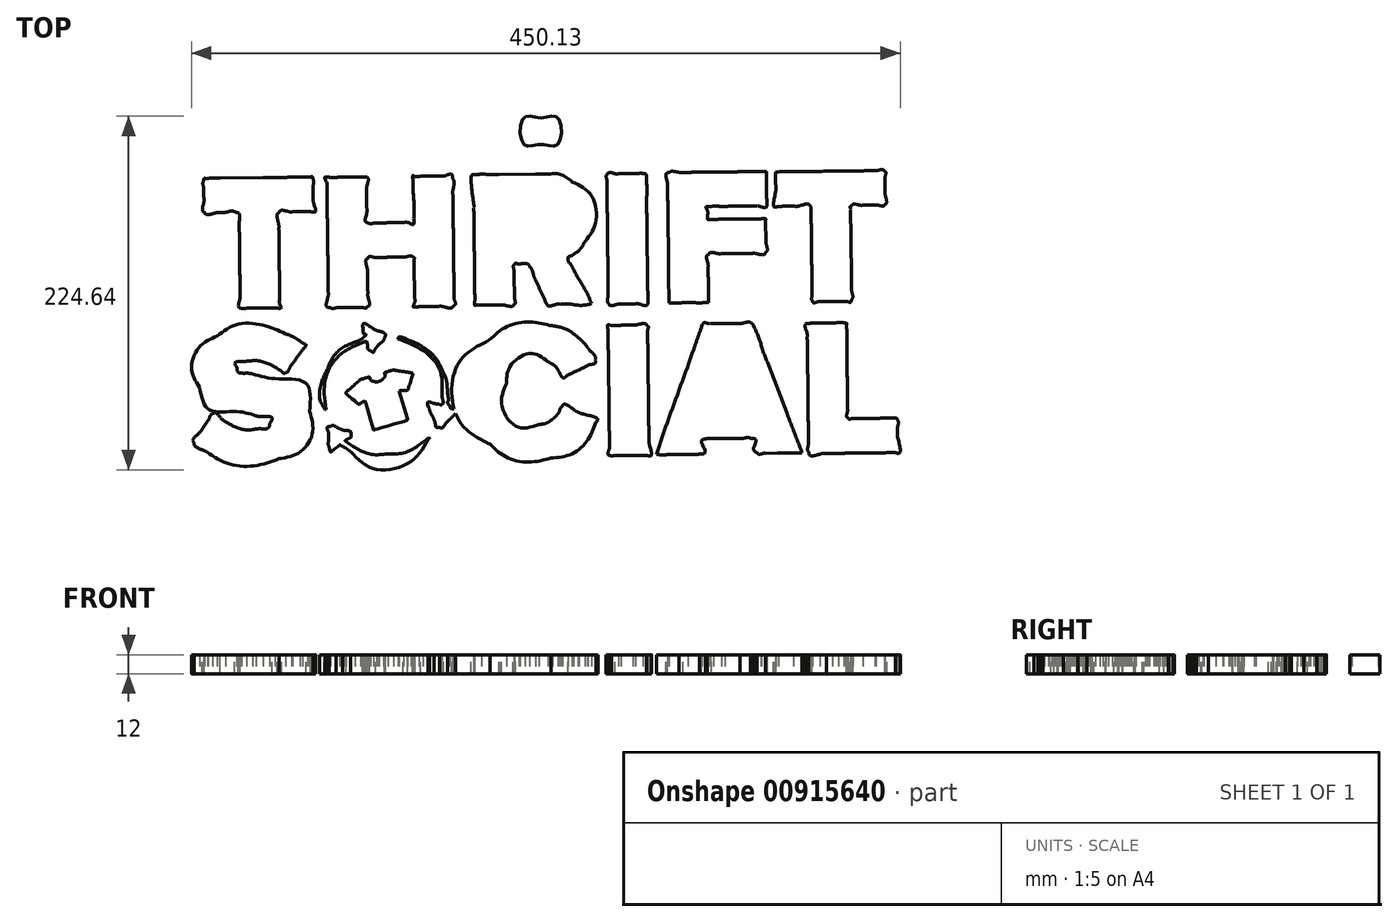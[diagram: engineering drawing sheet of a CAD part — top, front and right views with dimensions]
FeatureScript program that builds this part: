
annotation { "Feature Type Name" : "Feature", "Feature Type Description" : "" }
export const myFeature = defineFeature(function(context is Context, id is Id, definition is map)
    precondition{}
    {
        {
            var Q0;
            Q0=qCreatedBy(makeId("Top.planeOp"),FACE);
            var sketch = newSketch(context, id + "F0", { "sketchPlane" : qUnion([Q0])});
            skFitSpline(sketch, "E0", {"points": [v(237.45, -85.7) * mm, v(237.37, -79.29) * mm, v(237.62, -72.98) * mm, v(232.36, -68.27) * mm]});
            skFitSpline(sketch, "E1", {"points": [v(232.36, -68.27) * mm, v(225.56, -62.17) * mm, v(213.96, -64.54) * mm, v(205.7, -64.65) * mm]});
            skFitSpline(sketch, "E2", {"points": [v(205.7, -64.65) * mm, v(205.58, -55.22) * mm, v(205.46, -45.78) * mm, v(205.35, -36.34) * mm]});
            skFitSpline(sketch, "E3", {"points": [v(205.35, -36.34) * mm, v(205.3, -31.24) * mm, v(205.27, -26.12) * mm, v(205.19, -21.02) * mm]});
            skFitSpline(sketch, "E4", {"points": [v(205.19, -21.02) * mm, v(205.15, -18.88) * mm, v(204.58, -16.85) * mm, v(204.46, -14.77) * mm]});
            skFitSpline(sketch, "E5", {"points": [v(204.46, -14.77) * mm, v(204.35, -12.81) * mm, v(204.26, -14.2) * mm, v(205.06, -12.64) * mm]});
            skFitSpline(sketch, "E6", {"points": [v(205.06, -12.64) * mm, v(205.37, -12.05) * mm, v(205.87, -11.52) * mm, v(206.22, -10.94) * mm]});
            skFitSpline(sketch, "E7", {"points": [v(206.22, -10.94) * mm, v(208.27, -7.42) * mm, v(208.38, -3.67) * mm, v(208.32, 0.3) * mm]});
            skFitSpline(sketch, "E8", {"points": [v(208.32, 0.3) * mm, v(208.25, 4.7) * mm, v(208.24, 9.1) * mm, v(208.19, 13.51) * mm]});
            skFitSpline(sketch, "E9", {"points": [v(208.19, 13.51) * mm, v(208.08, 23.22) * mm, v(207.94, 32.92) * mm, v(207.82, 42.63) * mm]});
            skFitSpline(sketch, "E10", {"points": [v(207.82, 42.63) * mm, v(213.82, 42.68) * mm, v(219.81, 42.26) * mm, v(224.6, 46.51) * mm]});
            skFitSpline(sketch, "E11", {"points": [v(224.6, 46.51) * mm, v(228.54, 50.01) * mm, v(229.76, 54.8) * mm, v(229.7, 59.91) * mm, v(229.6, 70.09) * mm, v(232.36, 84.84) * mm, v(221.78, 90.83) * mm]});
            skFitSpline(sketch, "E12", {"points": [v(221.78, 90.83) * mm, v(216.17, 94) * mm, v(208.91, 92.77) * mm, v(202.73, 92.7) * mm]});
            skFitSpline(sketch, "E13", {"points": [v(202.73, 92.7) * mm, v(197.26, 92.62) * mm, v(191.78, 92.57) * mm, v(186.3, 92.5) * mm]});
            skFitSpline(sketch, "E14", {"points": [v(186.3, 92.5) * mm, v(179.32, 92.41) * mm, v(172.33, 92.32) * mm, v(165.34, 92.22) * mm]});
            skFitSpline(sketch, "E15", {"points": [v(165.34, 92.22) * mm, v(158.35, 92.13) * mm, v(151.35, 92.01) * mm, v(144.38, 91.73) * mm]});
            skFitSpline(sketch, "E16", {"points": [v(144.38, 91.73) * mm, v(141.8, 91.63) * mm, v(139.08, 92.28) * mm, v(136.39, 92.25) * mm]});
            skFitSpline(sketch, "E17", {"points": [v(136.39, 92.25) * mm, v(133.08, 92.2) * mm, v(129.77, 92.16) * mm, v(126.46, 92.11) * mm]});
            skFitSpline(sketch, "E18", {"points": [v(126.46, 92.11) * mm, v(112.57, 91.93) * mm, v(98.68, 91.78) * mm, v(84.79, 91.64) * mm]});
            skFitSpline(sketch, "E19", {"points": [v(84.79, 91.64) * mm, v(81.42, 91.6) * mm, v(77.86, 91.9) * mm, v(74.57, 91.06) * mm]});
            skFitSpline(sketch, "E20", {"points": [v(74.57, 91.06) * mm, v(73.32, 90.74) * mm, v(71.73, 89.56) * mm, v(70.54, 89.4) * mm]});
            skFitSpline(sketch, "E21", {"points": [v(70.54, 89.4) * mm, v(69.34, 89.25) * mm, v(67.88, 90.18) * mm, v(66.53, 90.52) * mm]});
            skFitSpline(sketch, "E22", {"points": [v(66.53, 90.52) * mm, v(60.3, 92.12) * mm, v(52.73, 90.87) * mm, v(46.32, 90.8) * mm, v(44.17, 90.77) * mm, v(42.6, 90.54) * mm, v(40.71, 91.48) * mm]});
            skFitSpline(sketch, "E23", {"points": [v(40.71, 91.48) * mm, v(37.97, 92.84) * mm, v(35.29, 94.33) * mm, v(32.58, 95.76) * mm]});
            skFitSpline(sketch, "E24", {"points": [v(32.58, 95.76) * mm, v(29.37, 97.45) * mm, v(26.16, 99.14) * mm, v(22.95, 100.83) * mm]});
            skFitSpline(sketch, "E25", {"points": [v(22.95, 100.83) * mm, v(21.58, 101.55) * mm, v(18.52, 102.46) * mm, v(17.52, 103.69) * mm]});
            skFitSpline(sketch, "E26", {"points": [v(17.52, 103.69) * mm, v(16.6, 104.82) * mm, v(16.34, 107.82) * mm, v(15.63, 109.26) * mm]});
            skFitSpline(sketch, "E27", {"points": [v(15.63, 109.26) * mm, v(14.35, 111.84) * mm, v(12.53, 114.14) * mm, v(10.34, 116) * mm]});
            skFitSpline(sketch, "E28", {"points": [v(10.34, 116) * mm, v(6.31, 119.4) * mm, v(1.07, 121.17) * mm, v(-4.18, 120.92) * mm]});
            skFitSpline(sketch, "E29", {"points": [v(-4.18, 120.92) * mm, v(-9.3, 120.68) * mm, v(-14.2, 118.52) * mm, v(-17.86, 114.94) * mm]});
            skFitSpline(sketch, "E30", {"points": [v(-17.86, 114.94) * mm, v(-19.65, 113.19) * mm, v(-21.13, 111.11) * mm, v(-22.2, 108.85) * mm]});
            skFitSpline(sketch, "E31", {"points": [v(-22.2, 108.85) * mm, v(-22.92, 107.29) * mm, v(-23.07, 104.5) * mm, v(-24.04, 103.27) * mm]});
            skFitSpline(sketch, "E32", {"points": [v(-24.04, 103.27) * mm, v(-25.28, 101.68) * mm, v(-28.46, 100.42) * mm, v(-30.14, 99.33) * mm]});
            skFitSpline(sketch, "E33", {"points": [v(-30.14, 99.33) * mm, v(-33.21, 97.35) * mm, v(-36.28, 95.38) * mm, v(-39.35, 93.4) * mm]});
            skFitSpline(sketch, "E34", {"points": [v(-39.35, 93.4) * mm, v(-40.9, 92.4) * mm, v(-42.75, 90.67) * mm, v(-44.5, 90.06) * mm]});
            skFitSpline(sketch, "E35", {"points": [v(-44.5, 90.06) * mm, v(-45.7, 89.66) * mm, v(-47.4, 89.84) * mm, v(-48.65, 89.53) * mm]});
            skFitSpline(sketch, "E36", {"points": [v(-48.65, 89.53) * mm, v(-49.89, 89.23) * mm, v(-51.05, 88.5) * mm, v(-52.25, 88.22) * mm]});
            skFitSpline(sketch, "E37", {"points": [v(-52.25, 88.22) * mm, v(-53.92, 87.84) * mm, v(-52.76, 87.94) * mm, v(-54.16, 88.18) * mm]});
            skFitSpline(sketch, "E38", {"points": [v(-54.16, 88.18) * mm, v(-54.8, 88.28) * mm, v(-55.58, 88.72) * mm, v(-56.24, 88.9) * mm]});
            skFitSpline(sketch, "E39", {"points": [v(-56.24, 88.9) * mm, v(-58.18, 89.43) * mm, v(-60.1, 89.45) * mm, v(-62.1, 89.43) * mm]});
            skFitSpline(sketch, "E40", {"points": [v(-62.1, 89.43) * mm, v(-69.08, 89.36) * mm, v(-76.1, 89.47) * mm, v(-83.08, 89.17) * mm]});
            skFitSpline(sketch, "E41", {"points": [v(-83.08, 89.17) * mm, v(-89.05, 88.92) * mm, v(-94.4, 85.9) * mm, v(-96.97, 80.38) * mm]});
            skFitSpline(sketch, "E42", {"points": [v(-96.97, 80.38) * mm, v(-97.46, 79.34) * mm, v(-97.38, 79.07) * mm, v(-98.26, 78.72) * mm]});
            skFitSpline(sketch, "E43", {"points": [v(-98.26, 78.72) * mm, v(-98.59, 78.58) * mm, v(-100.28, 78.57) * mm, v(-100.59, 78.72) * mm]});
            skFitSpline(sketch, "E44", {"points": [v(-100.59, 78.72) * mm, v(-101.26, 79.04) * mm, v(-101.72, 80.93) * mm, v(-102.2, 81.69) * mm]});
            skFitSpline(sketch, "E45", {"points": [v(-102.2, 81.69) * mm, v(-102.9, 82.8) * mm, v(-103.75, 83.83) * mm, v(-104.72, 84.73) * mm]});
            skFitSpline(sketch, "E46", {"points": [v(-104.72, 84.73) * mm, v(-109.36, 89.03) * mm, v(-115.12, 88.79) * mm, v(-121.04, 88.7) * mm]});
            skFitSpline(sketch, "E47", {"points": [v(-121.04, 88.7) * mm, v(-127.22, 88.6) * mm, v(-133.4, 88.58) * mm, v(-139.58, 88.44) * mm]});
            skFitSpline(sketch, "E48", {"points": [v(-139.58, 88.44) * mm, v(-140, 88.43) * mm, v(-140.67, 88.27) * mm, v(-141.07, 88.15) * mm]});
            skFitSpline(sketch, "E49", {"points": [v(-141.07, 88.15) * mm, v(-144.26, 87.2) * mm, v(-148.32, 88.72) * mm, v(-151.96, 88.67) * mm]});
            skFitSpline(sketch, "E50", {"points": [v(-151.96, 88.67) * mm, v(-171.27, 88.38) * mm, v(-190.58, 88.15) * mm, v(-209.9, 87.94) * mm]});
            skFitSpline(sketch, "E51", {"points": [v(-209.9, 87.94) * mm, v(-217.98, 87.85) * mm, v(-226.1, 88.6) * mm, v(-231.3, 76.87) * mm]});
            skFitSpline(sketch, "E52", {"points": [v(-231.3, 76.87) * mm, v(-231.94, 69.1) * mm, v(-231.59, 60.71) * mm, v(-231.2, 52.75) * mm]});
            skFitSpline(sketch, "E53", {"points": [v(-231.2, 52.75) * mm, v(-230.97, 47.98) * mm, v(-228.9, 43.5) * mm, v(-225, 40.65) * mm]});
            skFitSpline(sketch, "E54", {"points": [v(-225, 40.65) * mm, v(-220.14, 37.1) * mm, v(-214.44, 37.74) * mm, v(-208.76, 37.83) * mm]});
            skFitSpline(sketch, "E55", {"points": [v(-208.76, 37.83) * mm, v(-208.65, 27.45) * mm, v(-208.52, 17.06) * mm, v(-208.4, 6.68) * mm]});
            skFitSpline(sketch, "E56", {"points": [v(-208.4, 6.68) * mm, v(-208.35, 1.65) * mm, v(-208.62, -3.5) * mm, v(-208.21, -8.51) * mm]});
            skFitSpline(sketch, "E57", {"points": [v(-208.21, -8.51) * mm, v(-208.12, -9.69) * mm, v(-207.74, -10.09) * mm, v(-208.48, -10.77) * mm]});
            skFitSpline(sketch, "E58", {"points": [v(-208.48, -10.77) * mm, v(-209.04, -11.29) * mm, v(-210.44, -11.56) * mm, v(-211.13, -11.88) * mm]});
            skFitSpline(sketch, "E59", {"points": [v(-211.13, -11.88) * mm, v(-213.34, -12.88) * mm, v(-215.48, -14.04) * mm, v(-217.51, -15.37) * mm]});
            skFitSpline(sketch, "E60", {"points": [v(-217.51, -15.37) * mm, v(-230.73, -24) * mm, v(-237.84, -39.46) * mm, v(-235.49, -55.12) * mm]});
            skFitSpline(sketch, "E61", {"points": [v(-235.49, -55.12) * mm, v(-234.96, -58.61) * mm, v(-234, -62.03) * mm, v(-232.56, -65.25) * mm]});
            skFitSpline(sketch, "E62", {"points": [v(-232.56, -65.25) * mm, v(-231.7, -67.16) * mm, v(-230.68, -69) * mm, v(-229.5, -70.72) * mm]});
            skFitSpline(sketch, "E63", {"points": [v(-229.5, -70.72) * mm, v(-229.13, -71.26) * mm, v(-227.25, -73.1) * mm, v(-227.23, -73.68) * mm]});
            skFitSpline(sketch, "E64", {"points": [v(-227.23, -73.68) * mm, v(-227.2, -74.43) * mm, v(-229.05, -76.36) * mm, v(-229.44, -76.92) * mm]});
            skFitSpline(sketch, "E65", {"points": [v(-229.44, -76.92) * mm, v(-232.11, -80.84) * mm, v(-235.81, -85.02) * mm, v(-237.2, -89.63) * mm]});
            skFitSpline(sketch, "E66", {"points": [v(-237.2, -89.63) * mm, v(-242.1, -106.03) * mm, v(-218.44, -115.57) * mm, v(-206.41, -118.5) * mm]});
            skFitSpline(sketch, "E67", {"points": [v(-206.41, -118.5) * mm, v(-187.28, -123.15) * mm, v(-162.76, -122.06) * mm, v(-147.87, -107.64) * mm]});
            skFitSpline(sketch, "E68", {"points": [v(-147.87, -107.64) * mm, v(-144.82, -111.25) * mm, v(-140.15, -113.3) * mm, v(-135.43, -113.12) * mm]});
            skFitSpline(sketch, "E69", {"points": [v(-135.43, -113.12) * mm, v(-134.24, -113.08) * mm, v(-133.04, -112.9) * mm, v(-131.88, -112.58) * mm]});
            skFitSpline(sketch, "E70", {"points": [v(-131.88, -112.58) * mm, v(-130.1, -112.09) * mm, v(-130.21, -111.7) * mm, v(-128.58, -112.4) * mm]});
            skFitSpline(sketch, "E71", {"points": [v(-128.58, -112.4) * mm, v(-126.45, -113.32) * mm, v(-124.5, -114.75) * mm, v(-122.35, -115.69) * mm]});
            skFitSpline(sketch, "E72", {"points": [v(-122.35, -115.69) * mm, v(-109.58, -121.26) * mm, v(-94.53, -120.88) * mm, v(-81.82, -115.42) * mm]});
            skFitSpline(sketch, "E73", {"points": [v(-81.82, -115.42) * mm, v(-80.46, -114.83) * mm, v(-79.15, -114.14) * mm, v(-77.88, -113.37) * mm]});
            skFitSpline(sketch, "E74", {"points": [v(-77.88, -113.37) * mm, v(-72.74, -110.21) * mm, v(-67.34, -105.88) * mm, v(-63.48, -100.7) * mm]});
            skFitSpline(sketch, "E75", {"points": [v(-63.48, -100.7) * mm, v(-62.6, -99.5) * mm, v(-61.98, -98.14) * mm, v(-60.89, -97.25) * mm]});
            skFitSpline(sketch, "E76", {"points": [v(-60.89, -97.25) * mm, v(-59.3, -95.94) * mm, v(-57.34, -95.28) * mm, v(-55.76, -93.8) * mm]});
            skFitSpline(sketch, "E77", {"points": [v(-55.76, -93.8) * mm, v(-37.83, -119.87) * mm, v(2.4, -127.38) * mm, v(28, -108.14) * mm]});
            skFitSpline(sketch, "E78", {"points": [v(28, -108.14) * mm, v(32.02, -116.2) * mm, v(39.9, -116.59) * mm, v(47.86, -116.46) * mm]});
            skFitSpline(sketch, "E79", {"points": [v(47.86, -116.46) * mm, v(52.81, -116.39) * mm, v(57.77, -116.38) * mm, v(62.73, -116.3) * mm]});
            skFitSpline(sketch, "E80", {"points": [v(62.73, -116.3) * mm, v(66.12, -116.25) * mm, v(69.29, -115.58) * mm, v(72.74, -115.9) * mm]});
            skFitSpline(sketch, "E81", {"points": [v(72.74, -115.9) * mm, v(76.33, -116.24) * mm, v(79.96, -116.18) * mm, v(83.56, -115.85) * mm]});
            skFitSpline(sketch, "E82", {"points": [v(83.56, -115.85) * mm, v(93.02, -115) * mm, v(104.6, -117.99) * mm, v(110.6, -108.36) * mm]});
            skFitSpline(sketch, "E83", {"points": [v(110.6, -108.36) * mm, v(110.87, -107.93) * mm, v(111.19, -107.02) * mm, v(111.55, -106.61) * mm]});
            skFitSpline(sketch, "E84", {"points": [v(111.55, -106.61) * mm, v(112.6, -105.43) * mm, v(112.76, -105.67) * mm, v(114.58, -105.66) * mm]});
            skFitSpline(sketch, "E85", {"points": [v(114.58, -105.66) * mm, v(115.87, -105.64) * mm, v(117.16, -105.63) * mm, v(118.46, -105.62) * mm]});
            skFitSpline(sketch, "E86", {"points": [v(118.46, -105.62) * mm, v(120.23, -105.6) * mm, v(120.37, -105.35) * mm, v(121.42, -106.5) * mm]});
            skFitSpline(sketch, "E87", {"points": [v(121.42, -106.5) * mm, v(122.48, -107.63) * mm, v(123.04, -109.24) * mm, v(124.18, -110.4) * mm]});
            skFitSpline(sketch, "E88", {"points": [v(124.18, -110.4) * mm, v(125.7, -112) * mm, v(127.58, -113.22) * mm, v(129.64, -114.01) * mm]});
            skFitSpline(sketch, "E89", {"points": [v(129.64, -114.01) * mm, v(134.17, -115.74) * mm, v(139.1, -114.75) * mm, v(143.77, -115.03) * mm]});
            skFitSpline(sketch, "E90", {"points": [v(143.77, -115.03) * mm, v(146.14, -115.17) * mm, v(148.5, -115.08) * mm, v(150.87, -114.97) * mm]});
            skFitSpline(sketch, "E91", {"points": [v(150.87, -114.97) * mm, v(162.8, -114.43) * mm, v(174.77, -115.11) * mm, v(186.82, -114.99) * mm]});
            skFitSpline(sketch, "E92", {"points": [v(186.82, -114.99) * mm, v(190.81, -114.95) * mm, v(194.8, -114.9) * mm, v(198.8, -114.86) * mm]});
            skFitSpline(sketch, "E93", {"points": [v(198.8, -114.86) * mm, v(203.91, -114.8) * mm, v(209.03, -114.74) * mm, v(214.14, -114.67) * mm]});
            skFitSpline(sketch, "E94", {"points": [v(214.14, -114.67) * mm, v(219.16, -114.6) * mm, v(224.67, -115.22) * mm, v(229.3, -112.93) * mm]});
            skFitSpline(sketch, "E95", {"points": [v(229.3, -112.93) * mm, v(239.81, -107.74) * mm, v(237.57, -95.35) * mm, v(237.45, -85.7) * mm]});
            skFitSpline(sketch, "E96", {"points": [v(-169.5, -104.3) * mm, v(-184.03, -108.7) * mm, v(-201.82, -107.43) * mm, v(-215.22, -100.1) * mm]});
            skFitSpline(sketch, "E97", {"points": [v(-215.22, -100.1) * mm, v(-217.04, -99.1) * mm, v(-222.72, -96.5) * mm, v(-223.4, -94.41) * mm]});
            skFitSpline(sketch, "E98", {"points": [v(-223.4, -94.41) * mm, v(-224.13, -92.16) * mm, v(-219.57, -87.52) * mm, v(-218.25, -85.59) * mm]});
            skFitSpline(sketch, "E99", {"points": [v(-218.25, -85.59) * mm, v(-217.09, -83.89) * mm, v(-215.93, -82.18) * mm, v(-214.77, -80.48) * mm]});
            skFitSpline(sketch, "E100", {"points": [v(-214.77, -80.48) * mm, v(-214.12, -79.52) * mm, v(-212.76, -76.37) * mm, v(-211.6, -75.9) * mm]});
            skFitSpline(sketch, "E101", {"points": [v(-211.6, -75.9) * mm, v(-209.8, -75.16) * mm, v(-205.2, -79.76) * mm, v(-203.38, -80.77) * mm]});
            skFitSpline(sketch, "E102", {"points": [v(-203.38, -80.77) * mm, v(-197.56, -84.02) * mm, v(-190.4, -85.96) * mm, v(-183.7, -85.45) * mm]});
            skFitSpline(sketch, "E103", {"points": [v(-183.7, -85.45) * mm, v(-181.24, -85.26) * mm, v(-176.38, -84.97) * mm, v(-175.4, -82.06) * mm]});
            skFitSpline(sketch, "E104", {"points": [v(-175.4, -82.06) * mm, v(-174.05, -78.03) * mm, v(-181.49, -77.57) * mm, v(-183.9, -77.07) * mm]});
            skFitSpline(sketch, "E105", {"points": [v(-183.9, -77.07) * mm, v(-196.85, -74.39) * mm, v(-213.89, -73.12) * mm, v(-219.86, -59.08) * mm]});
            skFitSpline(sketch, "E106", {"points": [v(-219.86, -59.08) * mm, v(-225, -47) * mm, v(-219.75, -33.1) * mm, v(-208.69, -26.5) * mm]});
            skFitSpline(sketch, "E107", {"points": [v(-208.69, -26.5) * mm, v(-196.07, -19) * mm, v(-178.57, -19.8) * mm, v(-165.25, -24.97) * mm]});
            skFitSpline(sketch, "E108", {"points": [v(-165.25, -24.97) * mm, v(-162.09, -26.2) * mm, v(-159.06, -27.74) * mm, v(-156.2, -29.57) * mm]});
            skFitSpline(sketch, "E109", {"points": [v(-156.2, -29.57) * mm, v(-153.01, -31.62) * mm, v(-152.16, -31.98) * mm, v(-154.52, -35.2) * mm]});
            skFitSpline(sketch, "E110", {"points": [v(-154.52, -35.2) * mm, v(-156.85, -38.38) * mm, v(-159.2, -41.54) * mm, v(-161.53, -44.71) * mm]});
            skFitSpline(sketch, "E111", {"points": [v(-161.53, -44.71) * mm, v(-162.25, -45.7) * mm, v(-163.98, -49.06) * mm, v(-165.15, -49.55) * mm]});
            skFitSpline(sketch, "E112", {"points": [v(-165.15, -49.55) * mm, v(-166.52, -50.13) * mm, v(-167.86, -48.73) * mm, v(-169.03, -48.04) * mm]});
            skFitSpline(sketch, "E113", {"points": [v(-169.03, -48.04) * mm, v(-175.33, -44.34) * mm, v(-182.8, -42.13) * mm, v(-190.16, -42.42) * mm]});
            skFitSpline(sketch, "E114", {"points": [v(-190.16, -42.42) * mm, v(-192.3, -42.5) * mm, v(-197.37, -43.22) * mm, v(-196.2, -46.55) * mm]});
            skFitSpline(sketch, "E115", {"points": [v(-196.2, -46.55) * mm, v(-195.2, -49.47) * mm, v(-188.8, -50.03) * mm, v(-186.2, -50.55) * mm]});
            skFitSpline(sketch, "E116", {"points": [v(-186.2, -50.55) * mm, v(-171.68, -53.46) * mm, v(-152.42, -56.36) * mm, v(-150.06, -74.27) * mm]});
            skFitSpline(sketch, "E117", {"points": [v(-150.06, -74.27) * mm, v(-148.25, -87.95) * mm, v(-156.37, -100.3) * mm, v(-169.5, -104.3) * mm]});
            skFitSpline(sketch, "E118", {"points": [v(-149.46, 52.65) * mm, v(-153.23, 52.65) * mm, v(-157, 52.6) * mm, v(-160.78, 52.55) * mm]});
            skFitSpline(sketch, "E119", {"points": [v(-160.78, 52.55) * mm, v(-162.7, 52.53) * mm, v(-168.01, 53.44) * mm, v(-169.45, 51.94) * mm]});
            skFitSpline(sketch, "E120", {"points": [v(-169.45, 51.94) * mm, v(-170.73, 50.61) * mm, v(-169.61, 44.07) * mm, v(-169.59, 42.3) * mm]});
            skFitSpline(sketch, "E121", {"points": [v(-169.59, 42.3) * mm, v(-169.54, 38.57) * mm, v(-169.5, 34.85) * mm, v(-169.45, 31.12) * mm]});
            skFitSpline(sketch, "E122", {"points": [v(-169.45, 31.12) * mm, v(-169.36, 23.66) * mm, v(-169.27, 16.2) * mm, v(-169.2, 8.74) * mm]});
            skFitSpline(sketch, "E123", {"points": [v(-169.2, 8.74) * mm, v(-169.15, 4.96) * mm, v(-169.11, 1.2) * mm, v(-169.06, -2.58) * mm]});
            skFitSpline(sketch, "E124", {"points": [v(-169.06, -2.58) * mm, v(-169.01, -6.06) * mm, v(-168, -8.45) * mm, v(-172, -8.55) * mm]});
            skFitSpline(sketch, "E125", {"points": [v(-172, -8.55) * mm, v(-175.65, -8.64) * mm, v(-179.3, -8.6) * mm, v(-182.95, -8.65) * mm]});
            skFitSpline(sketch, "E126", {"points": [v(-182.95, -8.65) * mm, v(-186.36, -8.7) * mm, v(-189.76, -8.75) * mm, v(-193.16, -8.82) * mm]});
            skFitSpline(sketch, "E127", {"points": [v(-193.16, -8.82) * mm, v(-195.24, -7.83) * mm, v(-194.19, -2.27) * mm, v(-194.2, -0.21) * mm]});
            skFitSpline(sketch, "E128", {"points": [v(-194.2, -0.21) * mm, v(-194.25, 3.55) * mm, v(-194.3, 7.3) * mm, v(-194.33, 11.07) * mm]});
            skFitSpline(sketch, "E129", {"points": [v(-194.33, 11.07) * mm, v(-194.42, 18.58) * mm, v(-194.5, 26.1) * mm, v(-194.59, 33.62) * mm]});
            skFitSpline(sketch, "E130", {"points": [v(-194.59, 33.62) * mm, v(-194.63, 37.38) * mm, v(-194.67, 41.14) * mm, v(-194.7, 44.9) * mm]});
            skFitSpline(sketch, "E131", {"points": [v(-194.7, 44.9) * mm, v(-194.72, 46.17) * mm, v(-194.46, 47.8) * mm, v(-194.54, 49.21) * mm]});
            skFitSpline(sketch, "E132", {"points": [v(-194.54, 49.21) * mm, v(-194.63, 50.61) * mm, v(-195.07, 51.8) * mm, v(-196.49, 52.16) * mm]});
            skFitSpline(sketch, "E133", {"points": [v(-196.49, 52.16) * mm, v(-199.58, 52.95) * mm, v(-204.12, 52.03) * mm, v(-207.33, 51.98) * mm]});
            skFitSpline(sketch, "E134", {"points": [v(-207.33, 51.98) * mm, v(-209.27, 51.95) * mm, v(-215.39, 50.77) * mm, v(-216.77, 52.14) * mm]});
            skFitSpline(sketch, "E135", {"points": [v(-216.77, 52.14) * mm, v(-218.06, 53.43) * mm, v(-217.16, 58.96) * mm, v(-217.19, 60.73) * mm]});
            skFitSpline(sketch, "E136", {"points": [v(-217.19, 60.73) * mm, v(-217.21, 62.5) * mm, v(-217.25, 64.26) * mm, v(-217.29, 66.03) * mm]});
            skFitSpline(sketch, "E137", {"points": [v(-217.29, 66.03) * mm, v(-217.32, 67.73) * mm, v(-217.88, 70.35) * mm, v(-217.43, 71.98) * mm]});
            skFitSpline(sketch, "E138", {"points": [v(-217.43, 71.98) * mm, v(-216.94, 73.8) * mm, v(-216.2, 73.73) * mm, v(-214.58, 73.77) * mm]});
            skFitSpline(sketch, "E139", {"points": [v(-214.58, 73.77) * mm, v(-212.04, 73.84) * mm, v(-209.5, 73.8) * mm, v(-206.95, 73.89) * mm]});
            skFitSpline(sketch, "E140", {"points": [v(-206.95, 73.89) * mm, v(-197.85, 74.03) * mm, v(-188.74, 74.16) * mm, v(-179.63, 74.3) * mm]});
            skFitSpline(sketch, "E141", {"points": [v(-179.63, 74.3) * mm, v(-170.17, 74.22) * mm, v(-160.7, 74.51) * mm, v(-151.23, 74.56) * mm]});
            skFitSpline(sketch, "E142", {"points": [v(-151.23, 74.56) * mm, v(-149.73, 74.57) * mm, v(-148.42, 74.88) * mm, v(-147.88, 73.2) * mm]});
            skFitSpline(sketch, "E143", {"points": [v(-147.88, 73.2) * mm, v(-147.35, 71.56) * mm, v(-147.83, 68.9) * mm, v(-147.81, 67.19) * mm]});
            skFitSpline(sketch, "E144", {"points": [v(-147.81, 67.19) * mm, v(-147.8, 65.07) * mm, v(-147.77, 62.94) * mm, v(-147.74, 60.82) * mm]});
            skFitSpline(sketch, "E145", {"points": [v(-147.74, 60.82) * mm, v(-147.7, 58.78) * mm, v(-146.23, 52.64) * mm, v(-149.46, 52.65) * mm]});
            skFitSpline(sketch, "E146", {"points": [v(-137, 74.37) * mm, v(-133.2, 74.42) * mm, v(-129.4, 74.45) * mm, v(-125.6, 74.5) * mm]});
            skFitSpline(sketch, "E147", {"points": [v(-125.6, 74.5) * mm, v(-122.04, 74.55) * mm, v(-118.48, 74.6) * mm, v(-114.92, 74.68) * mm]});
            skFitSpline(sketch, "E148", {"points": [v(-114.92, 74.68) * mm, v(-112.8, 73.7) * mm, v(-113.89, 67.74) * mm, v(-113.86, 65.59) * mm]});
            skFitSpline(sketch, "E149", {"points": [v(-113.86, 65.59) * mm, v(-113.8, 61.71) * mm, v(-113.74, 57.84) * mm, v(-113.7, 53.97) * mm]});
            skFitSpline(sketch, "E150", {"points": [v(-113.7, 53.97) * mm, v(-113.67, 52.07) * mm, v(-114.65, 46.45) * mm, v(-112.7, 45.43) * mm, v(-111.67, 44.9) * mm, v(-109.32, 45.37) * mm, v(-108.24, 45.4) * mm]});
            skFitSpline(sketch, "E151", {"points": [v(-108.24, 45.4) * mm, v(-105.97, 45.44) * mm, v(-103.69, 45.48) * mm, v(-101.4, 45.52) * mm]});
            skFitSpline(sketch, "E152", {"points": [v(-101.4, 45.52) * mm, v(-97.76, 45.58) * mm, v(-94.12, 45.62) * mm, v(-90.47, 45.66) * mm]});
            skFitSpline(sketch, "E153", {"points": [v(-90.47, 45.66) * mm, v(-87.46, 45.69) * mm, v(-84.08, 44.55) * mm, v(-83.93, 48.22) * mm]});
            skFitSpline(sketch, "E154", {"points": [v(-83.93, 48.22) * mm, v(-83.62, 55.92) * mm, v(-84.16, 63.76) * mm, v(-84.3, 71.46) * mm]});
            skFitSpline(sketch, "E155", {"points": [v(-84.3, 71.46) * mm, v(-84.36, 75.55) * mm, v(-83.3, 75.05) * mm, v(-79.42, 75.09) * mm]});
            skFitSpline(sketch, "E156", {"points": [v(-79.42, 75.09) * mm, v(-75.21, 75.13) * mm, v(-71, 75.18) * mm, v(-66.78, 75.24) * mm]});
            skFitSpline(sketch, "E157", {"points": [v(-66.78, 75.24) * mm, v(-64.22, 75.27) * mm, v(-59.98, 76.5) * mm, v(-59.13, 73.73) * mm]});
            skFitSpline(sketch, "E158", {"points": [v(-59.13, 73.73) * mm, v(-58.21, 70.77) * mm, v(-59.04, 66.1) * mm, v(-59, 62.98) * mm]});
            skFitSpline(sketch, "E159", {"points": [v(-59, 62.98) * mm, v(-58.91, 55.12) * mm, v(-58.83, 47.27) * mm, v(-58.75, 39.4) * mm]});
            skFitSpline(sketch, "E160", {"points": [v(-58.75, 39.4) * mm, v(-58.66, 31.3) * mm, v(-58.57, 23.19) * mm, v(-58.47, 15.08) * mm]});
            skFitSpline(sketch, "E161", {"points": [v(-58.47, 15.08) * mm, v(-58.43, 11.37) * mm, v(-58.39, 7.66) * mm, v(-58.33, 3.95) * mm]});
            skFitSpline(sketch, "E162", {"points": [v(-58.33, 3.95) * mm, v(-58.3, 2.1) * mm, v(-58.27, 0.24) * mm, v(-58.23, -1.62) * mm]});
            skFitSpline(sketch, "E163", {"points": [v(-58.23, -1.62) * mm, v(-58.2, -2.92) * mm, v(-57.4, -6.18) * mm, v(-58.5, -7.15) * mm]});
            skFitSpline(sketch, "E164", {"points": [v(-58.5, -7.15) * mm, v(-60.11, -8.57) * mm, v(-66, -7.55) * mm, v(-68.1, -7.57) * mm]});
            skFitSpline(sketch, "E165", {"points": [v(-68.1, -7.57) * mm, v(-70.18, -7.6) * mm, v(-72.26, -7.65) * mm, v(-74.34, -7.7) * mm]});
            skFitSpline(sketch, "E166", {"points": [v(-74.34, -7.7) * mm, v(-76.42, -7.73) * mm, v(-78.5, -7.77) * mm, v(-80.57, -7.75) * mm]});
            skFitSpline(sketch, "E167", {"points": [v(-80.57, -7.75) * mm, v(-84.3, -7.72) * mm, v(-83.32, -5.38) * mm, v(-83.37, -2.15) * mm]});
            skFitSpline(sketch, "E168", {"points": [v(-83.37, -2.15) * mm, v(-83.42, 1.94) * mm, v(-83.49, 6.02) * mm, v(-83.54, 10.11) * mm]});
            skFitSpline(sketch, "E169", {"points": [v(-83.54, 10.11) * mm, v(-83.6, 13.78) * mm, v(-83.57, 17.46) * mm, v(-83.66, 21.14) * mm]});
            skFitSpline(sketch, "E170", {"points": [v(-83.66, 21.14) * mm, v(-83.68, 22.15) * mm, v(-83.4, 23.24) * mm, v(-84.37, 23.8) * mm]});
            skFitSpline(sketch, "E171", {"points": [v(-84.37, 23.8) * mm, v(-85.68, 24.55) * mm, v(-89.15, 23.8) * mm, v(-90.67, 23.77) * mm]});
            skFitSpline(sketch, "E172", {"points": [v(-90.67, 23.77) * mm, v(-94.44, 23.7) * mm, v(-98.2, 23.65) * mm, v(-101.98, 23.6) * mm]});
            skFitSpline(sketch, "E173", {"points": [v(-101.98, 23.6) * mm, v(-103.86, 23.57) * mm, v(-105.74, 23.55) * mm, v(-107.63, 23.53) * mm]});
            skFitSpline(sketch, "E174", {"points": [v(-107.63, 23.53) * mm, v(-108.89, 23.51) * mm, v(-112.1, 24.1) * mm, v(-113.04, 23.1) * mm]});
            skFitSpline(sketch, "E175", {"points": [v(-113.04, 23.1) * mm, v(-114.32, 21.73) * mm, v(-113.22, 15.28) * mm, v(-113.2, 13.41) * mm]});
            skFitSpline(sketch, "E176", {"points": [v(-113.2, 13.41) * mm, v(-113.15, 9.16) * mm, v(-113.1, 4.92) * mm, v(-113.05, 0.67) * mm]});
            skFitSpline(sketch, "E177", {"points": [v(-113.05, 0.67) * mm, v(-113.02, -1.3) * mm, v(-111.94, -6.5) * mm, v(-113.48, -7.95) * mm]});
            skFitSpline(sketch, "E178", {"points": [v(-113.48, -7.95) * mm, v(-114.24, -8.66) * mm, v(-116.43, -8.19) * mm, v(-117.38, -8.2) * mm]});
            skFitSpline(sketch, "E179", {"points": [v(-117.38, -8.2) * mm, v(-119.64, -8.21) * mm, v(-121.9, -8.23) * mm, v(-124.17, -8.26) * mm, v(-126.44, -8.28) * mm, v(-128.7, -8.31) * mm, v(-130.97, -8.35) * mm]});
            skFitSpline(sketch, "E180", {"points": [v(-130.97, -8.35) * mm, v(-132.57, -8.37) * mm, v(-135.32, -8.94) * mm, v(-136.83, -8.4) * mm]});
            skFitSpline(sketch, "E181", {"points": [v(-136.83, -8.4) * mm, v(-139.37, -7.5) * mm, v(-138.2, -0.8) * mm, v(-138.22, 1.59) * mm]});
            skFitSpline(sketch, "E182", {"points": [v(-138.22, 1.59) * mm, v(-138.3, 10.29) * mm, v(-138.4, 18.99) * mm, v(-138.5, 27.69) * mm]});
            skFitSpline(sketch, "E183", {"points": [v(-138.5, 27.69) * mm, v(-138.6, 36.73) * mm, v(-138.74, 45.78) * mm, v(-138.86, 54.83) * mm]});
            skFitSpline(sketch, "E184", {"points": [v(-138.86, 54.83) * mm, v(-138.92, 59.25) * mm, v(-138.98, 63.67) * mm, v(-139.04, 68.1) * mm]});
            skFitSpline(sketch, "E185", {"points": [v(-139.04, 68.1) * mm, v(-139.07, 70.76) * mm, v(-140.38, 74.33) * mm, v(-137, 74.37) * mm]});
            skFitSpline(sketch, "E186", {"points": [v(-87.99, -78.97) * mm, v(-87.81, -79.58) * mm, v(-88.06, -79.98) * mm, v(-88.73, -80.18) * mm, v(-88.74, -80.18) * mm, v(-88.78, -80.2) * mm, v(-108.5, -85.88) * mm, v(-108.55, -85.9) * mm, v(-108.55, -85.9) * mm, v(-109.16, -86.07) * mm, v(-109.56, -85.85) * mm, v(-109.73, -85.24) * mm, v(-109.73, -85.24) * mm, v(-109.74, -85.2) * mm, v(-114.75, -67.68) * mm, v(-114.81, -67.45) * mm, v(-114.81, -67.45) * mm, v(-114.81, -67.45) * mm]});
            skFitSpline(sketch, "E187", {"points": [v(-114.81, -67.45) * mm, v(-114.82, -67.45) * mm, v(-114.82, -67.45) * mm, v(-114.9, -67.5) * mm, v(-118.22, -69.42) * mm, v(-118.24, -69.43) * mm, v(-118.24, -69.43) * mm, v(-118.62, -69.73) * mm, v(-118.99, -69.7) * mm, v(-119.36, -69.35) * mm, v(-119.36, -69.35) * mm, v(-119.4, -69.32) * mm, v(-126.54, -63.31) * mm, v(-126.57, -63.3) * mm, v(-126.58, -63.29) * mm, v(-126.77, -63.08) * mm, v(-126.87, -62.84) * mm, v(-126.87, -62.58) * mm]});
            skFitSpline(sketch, "E188", {"points": [v(-126.87, -62.58) * mm, v(-126.9, -62.26) * mm, v(-126.78, -62) * mm, v(-126.5, -61.79) * mm, v(-126.5, -61.78) * mm, v(-126.47, -61.75) * mm, v(-117.78, -54.07) * mm, v(-117.67, -53.97) * mm, v(-117.67, -53.97) * mm, v(-117.67, -53.97) * mm]});
            skFitSpline(sketch, "E189", {"points": [v(-117.67, -53.97) * mm, v(-117.67, -53.97) * mm, v(-117.67, -53.97) * mm, v(-117.54, -53.94) * mm, v(-112.88, -52.6) * mm, v(-112.88, -52.6) * mm, v(-112.87, -52.6) * mm, v(-112.26, -52.42) * mm, v(-111.87, -52.63) * mm, v(-111.7, -53.24) * mm]});
            skFitSpline(sketch, "E190", {"points": [v(-111.7, -53.24) * mm, v(-111.43, -54.16) * mm, v(-110.7, -54.8) * mm, v(-109.5, -55.14) * mm]});
            skFitSpline(sketch, "E191", {"points": [v(-109.5, -55.14) * mm, v(-108.3, -55.5) * mm, v(-107.17, -55.51) * mm, v(-106.1, -55.2) * mm]});
            skFitSpline(sketch, "E192", {"points": [v(-106.1, -55.2) * mm, v(-105.02, -54.9) * mm, v(-104.05, -54.27) * mm, v(-103.2, -53.32) * mm]});
            skFitSpline(sketch, "E193", {"points": [v(-103.2, -53.32) * mm, v(-102.33, -52.38) * mm, v(-102.03, -51.45) * mm, v(-102.3, -50.53) * mm]});
            skFitSpline(sketch, "E194", {"points": [v(-102.3, -50.53) * mm, v(-102.47, -49.93) * mm, v(-102.25, -49.53) * mm, v(-101.64, -49.35) * mm, v(-101.63, -49.35) * mm, v(-101.63, -49.35) * mm, v(-96.97, -48) * mm, v(-96.84, -47.97) * mm, v(-96.84, -47.97) * mm, v(-96.84, -47.97) * mm]});
            skFitSpline(sketch, "E195", {"points": [v(-96.84, -47.97) * mm, v(-96.84, -47.97) * mm, v(-96.84, -47.97) * mm, v(-96.7, -48) * mm, v(-85.4, -49.81) * mm, v(-85.35, -49.82) * mm, v(-85.34, -49.82) * mm, v(-85, -49.85) * mm, v(-84.76, -50.02) * mm, v(-84.6, -50.3) * mm]});
            skFitSpline(sketch, "E196", {"points": [v(-84.6, -50.3) * mm, v(-84.48, -50.53) * mm, v(-84.46, -50.82) * mm, v(-84.56, -51.17) * mm, v(-84.56, -51.18) * mm, v(-84.57, -51.21) * mm, v(-87.47, -60.13) * mm, v(-87.48, -60.16) * mm, v(-87.48, -60.16) * mm, v(-87.58, -60.52) * mm, v(-87.84, -60.76) * mm, v(-88.27, -60.88) * mm]});
            skFitSpline(sketch, "E197", {"points": [v(-88.27, -60.88) * mm, v(-88.45, -60.94) * mm, v(-88.6, -60.95) * mm, v(-88.75, -60.93) * mm, v(-88.75, -60.93) * mm, v(-88.79, -60.93) * mm, v(-92.96, -61.17) * mm, v(-93.07, -61.18) * mm, v(-93.07, -61.18) * mm, v(-93.07, -61.18) * mm]});
            skFitSpline(sketch, "E198", {"points": [v(-93.07, -61.18) * mm, v(-93.07, -61.18) * mm, v(-93.07, -61.18) * mm, v(-93, -61.4) * mm, v(-88.05, -78.74) * mm, v(-87.99, -78.97) * mm, v(-87.99, -78.97) * mm, v(-87.99, -78.97) * mm]});
            skFitSpline(sketch, "E199", {"points": [v(-140.1, -73) * mm, v(-143.69, -65.5) * mm, v(-142.17, -55.1) * mm, v(-138.83, -47.81) * mm]});
            skFitSpline(sketch, "E200", {"points": [v(-138.83, -47.81) * mm, v(-135.32, -40.12) * mm, v(-128.95, -33.71) * mm, v(-121.2, -30.3) * mm]});
            skFitSpline(sketch, "E201", {"points": [v(-121.2, -30.3) * mm, v(-119.65, -29.62) * mm, v(-116.64, -28.05) * mm, v(-115.6, -26.93) * mm]});
            skFitSpline(sketch, "E202", {"points": [v(-115.6, -26.93) * mm, v(-114.22, -25.44) * mm, v(-116.03, -24.6) * mm, v(-115.95, -22.87) * mm]});
            skFitSpline(sketch, "E203", {"points": [v(-115.95, -22.87) * mm, v(-115.75, -18.46) * mm, v(-108.36, -22.42) * mm, v(-105.94, -23.23) * mm]});
            skFitSpline(sketch, "E204", {"points": [v(-105.94, -23.23) * mm, v(-104.9, -23.58) * mm, v(-103.73, -23.84) * mm, v(-102.94, -24.34) * mm]});
            skFitSpline(sketch, "E205", {"points": [v(-102.94, -24.34) * mm, v(-102.15, -24.85) * mm, v(-101.74, -25.6) * mm, v(-102.21, -26.91) * mm]});
            skFitSpline(sketch, "E206", {"points": [v(-102.21, -26.91) * mm, v(-102.96, -28.98) * mm, v(-105.72, -31.4) * mm, v(-107.13, -33.09) * mm]});
            skFitSpline(sketch, "E207", {"points": [v(-107.13, -33.09) * mm, v(-108.19, -34.35) * mm, v(-109.55, -36.7) * mm, v(-111.4, -35.6) * mm]});
            skFitSpline(sketch, "E208", {"points": [v(-111.4, -35.6) * mm, v(-112.95, -34.7) * mm, v(-113.42, -31.08) * mm, v(-113.9, -29.6) * mm]});
            skFitSpline(sketch, "E209", {"points": [v(-113.9, -29.6) * mm, v(-130.83, -38.37) * mm, v(-140.09, -54) * mm, v(-139.65, -73.05) * mm]});
            skFitSpline(sketch, "E210", {"points": [v(-139.65, -73.05) * mm, v(-139.8, -73.03) * mm, v(-139.96, -73.01) * mm, v(-140.1, -73) * mm]});
            skFitSpline(sketch, "E211", {"points": [v(-74.83, -92.3) * mm, v(-86.4, -106.55) * mm, v(-108.88, -110.72) * mm, v(-123.98, -99.81) * mm]});
            skFitSpline(sketch, "E212", {"points": [v(-123.98, -99.81) * mm, v(-125.64, -98.61) * mm, v(-127.21, -97.52) * mm, v(-128.97, -96.63) * mm]});
            skFitSpline(sketch, "E213", {"points": [v(-128.97, -96.63) * mm, v(-131.03, -95.59) * mm, v(-131.46, -96.06) * mm, v(-133.18, -97.37) * mm]});
            skFitSpline(sketch, "E214", {"points": [v(-133.18, -97.37) * mm, v(-135, -98.76) * mm, v(-136.69, -99.98) * mm, v(-137.54, -97.24) * mm]});
            skFitSpline(sketch, "E215", {"points": [v(-137.54, -97.24) * mm, v(-138.25, -94.93) * mm, v(-137.88, -91.78) * mm, v(-137.98, -89.38) * mm]});
            skFitSpline(sketch, "E216", {"points": [v(-137.98, -89.38) * mm, v(-138.05, -87.63) * mm, v(-138.9, -84.35) * mm, v(-136.7, -83.7) * mm]});
            skFitSpline(sketch, "E217", {"points": [v(-136.7, -83.7) * mm, v(-135, -83.2) * mm, v(-131.11, -85.28) * mm, v(-129.46, -85.84) * mm]});
            skFitSpline(sketch, "E218", {"points": [v(-129.46, -85.84) * mm, v(-128.1, -86.31) * mm, v(-124.1, -86.98) * mm, v(-123.88, -88.83) * mm]});
            skFitSpline(sketch, "E219", {"points": [v(-123.88, -88.83) * mm, v(-123.69, -90.5) * mm, v(-126.58, -92.2) * mm, v(-127.6, -93.03) * mm]});
            skFitSpline(sketch, "E220", {"points": [v(-127.6, -93.03) * mm, v(-119.47, -98.18) * mm, v(-110.1, -101.65) * mm, v(-100.37, -101.2) * mm]});
            skFitSpline(sketch, "E221", {"points": [v(-100.37, -101.2) * mm, v(-90.74, -100.73) * mm, v(-81.81, -96.49) * mm, v(-74.23, -90.73) * mm]});
            skFitSpline(sketch, "E222", {"points": [v(-74.23, -90.73) * mm, v(-73.91, -91.25) * mm, v(-74.46, -91.85) * mm, v(-74.83, -92.3) * mm]});
            skFitSpline(sketch, "E223", {"points": [v(-57.03, -75.4) * mm, v(-58.76, -77.16) * mm, v(-60.52, -78.88) * mm, v(-62.3, -80.58) * mm]});
            skFitSpline(sketch, "E224", {"points": [v(-62.3, -80.58) * mm, v(-63.57, -81.78) * mm, v(-65.62, -84.66) * mm, v(-67.59, -84.47) * mm]});
            skFitSpline(sketch, "E225", {"points": [v(-67.59, -84.47) * mm, v(-69.66, -84.27) * mm, v(-70.32, -81.26) * mm, v(-70.98, -79.73) * mm]});
            skFitSpline(sketch, "E226", {"points": [v(-70.98, -79.73) * mm, v(-71.95, -77.46) * mm, v(-73.26, -75.07) * mm, v(-73.9, -72.69) * mm]});
            skFitSpline(sketch, "E227", {"points": [v(-73.9, -72.69) * mm, v(-75.03, -68.45) * mm, v(-71.4, -69.1) * mm, v(-68.42, -69.62) * mm, v(-67.7, -69.75) * mm, v(-66.47, -70.3) * mm, v(-65.89, -69.68) * mm]});
            skFitSpline(sketch, "E228", {"points": [v(-65.89, -69.68) * mm, v(-65.1, -68.83) * mm, v(-65.84, -65.52) * mm, v(-65.92, -64.64) * mm]});
            skFitSpline(sketch, "E229", {"points": [v(-65.92, -64.64) * mm, v(-67.52, -47.46) * mm, v(-78.62, -35.25) * mm, v(-93.78, -28.3) * mm]});
            skFitSpline(sketch, "E230", {"points": [v(-93.78, -28.3) * mm, v(-93.1, -26.9) * mm, v(-86.72, -29.22) * mm, v(-85.48, -29.67) * mm]});
            skFitSpline(sketch, "E231", {"points": [v(-85.48, -29.67) * mm, v(-82.76, -30.66) * mm, v(-80.19, -32.01) * mm, v(-77.83, -33.7) * mm]});
            skFitSpline(sketch, "E232", {"points": [v(-77.83, -33.7) * mm, v(-72.85, -37.27) * mm, v(-68.67, -42.29) * mm, v(-66.03, -47.82) * mm]});
            skFitSpline(sketch, "E233", {"points": [v(-66.03, -47.82) * mm, v(-63.53, -53.07) * mm, v(-62.64, -58.84) * mm, v(-62.14, -64.63) * mm]});
            skFitSpline(sketch, "E234", {"points": [v(-62.14, -64.63) * mm, v(-61.88, -67.63) * mm, v(-62.52, -68.43) * mm, v(-60.93, -70.97) * mm]});
            skFitSpline(sketch, "E235", {"points": [v(-60.93, -70.97) * mm, v(-59.98, -72.47) * mm, v(-54.23, -72.56) * mm, v(-57.03, -75.4) * mm]});
            skFitSpline(sketch, "E236", {"points": [v(-3.2, 112.16) * mm, v(7.67, 112.16) * mm, v(7.64, 95.3) * mm, v(-3.2, 95.3) * mm, v(-14.03, 95.3) * mm, v(-14.08, 112.16) * mm, v(-3.2, 112.16) * mm]});
            skFitSpline(sketch, "E237", {"points": [v(-45.15, 75.91) * mm, v(-40.07, 76.42) * mm, v(-34.77, 76.06) * mm, v(-29.67, 76.11) * mm]});
            skFitSpline(sketch, "E238", {"points": [v(-29.67, 76.11) * mm, v(-22, 76.2) * mm, v(-14.32, 76.3) * mm, v(-6.65, 76.38) * mm]});
            skFitSpline(sketch, "E239", {"points": [v(-6.65, 76.38) * mm, v(1.53, 76.48) * mm, v(9.66, 76.24) * mm, v(16.71, 71.43) * mm]});
            skFitSpline(sketch, "E240", {"points": [v(16.71, 71.43) * mm, v(28.6, 63.33) * mm, v(31.76, 46) * mm, v(24.84, 33.64) * mm]});
            skFitSpline(sketch, "E241", {"points": [v(24.84, 33.64) * mm, v(23.02, 30.38) * mm, v(20.53, 27.57) * mm, v(17.5, 25.4) * mm]});
            skFitSpline(sketch, "E242", {"points": [v(17.5, 25.4) * mm, v(16.5, 24.67) * mm, v(14.42, 24.02) * mm, v(14.23, 22.67) * mm]});
            skFitSpline(sketch, "E243", {"points": [v(14.23, 22.67) * mm, v(14.05, 21.42) * mm, v(16.2, 18.59) * mm, v(16.79, 17.48) * mm]});
            skFitSpline(sketch, "E244", {"points": [v(16.79, 17.48) * mm, v(20.89, 9.78) * mm, v(25.47, 2.14) * mm, v(29.02, -5.83) * mm]});
            skFitSpline(sketch, "E245", {"points": [v(29.02, -5.83) * mm, v(22.61, -6.9) * mm, v(15.49, -6.14) * mm, v(8.99, -6.22) * mm]});
            skFitSpline(sketch, "E246", {"points": [v(8.99, -6.22) * mm, v(6.68, -6.25) * mm, v(1.76, -7.28) * mm, v(0.2, -5.53) * mm]});
            skFitSpline(sketch, "E247", {"points": [v(0.2, -5.53) * mm, v(-2.02, -0.62) * mm, v(-4.25, 4.29) * mm, v(-6.47, 9.2) * mm]});
            skFitSpline(sketch, "E248", {"points": [v(-6.47, 9.2) * mm, v(-7.75, 12.03) * mm, v(-8.74, 15.61) * mm, v(-10.5, 18.16) * mm]});
            skFitSpline(sketch, "E249", {"points": [v(-10.5, 18.16) * mm, v(-11.23, 19.22) * mm, v(-12.24, 19.55) * mm, v(-13.36, 19.62) * mm]});
            skFitSpline(sketch, "E250", {"points": [v(-13.36, 19.62) * mm, v(-14.48, 19.69) * mm, v(-15.72, 19.5) * mm, v(-16.9, 19.5) * mm]});
            skFitSpline(sketch, "E251", {"points": [v(-16.9, 19.5) * mm, v(-17.9, 19.5) * mm, v(-19.32, 19.82) * mm, v(-20, 18.93) * mm]});
            skFitSpline(sketch, "E252", {"points": [v(-20, 18.93) * mm, v(-20.7, 18.01) * mm, v(-20.17, 14.98) * mm, v(-20.15, 13.9) * mm]});
            skFitSpline(sketch, "E253", {"points": [v(-20.15, 13.9) * mm, v(-20.1, 10.54) * mm, v(-20.06, 7.17) * mm, v(-20.01, 3.8) * mm]});
            skFitSpline(sketch, "E254", {"points": [v(-20.01, 3.8) * mm, v(-19.99, 2) * mm, v(-19.96, 0.2) * mm, v(-19.93, -1.6) * mm]});
            skFitSpline(sketch, "E255", {"points": [v(-19.93, -1.6) * mm, v(-19.91, -2.56) * mm, v(-19.35, -5.37) * mm, v(-20.18, -6.23) * mm]});
            skFitSpline(sketch, "E256", {"points": [v(-20.18, -6.23) * mm, v(-21.44, -7.54) * mm, v(-27.26, -6.64) * mm, v(-29.05, -6.66) * mm]});
            skFitSpline(sketch, "E257", {"points": [v(-29.05, -6.66) * mm, v(-32.97, -6.7) * mm, v(-36.9, -6.76) * mm, v(-40.83, -6.82) * mm]});
            skFitSpline(sketch, "E258", {"points": [v(-40.83, -6.82) * mm, v(-44.53, -6.88) * mm, v(-45.04, -7) * mm, v(-45.08, -3.19) * mm]});
            skFitSpline(sketch, "E259", {"points": [v(-45.08, -3.19) * mm, v(-45.12, 0.73) * mm, v(-45.17, 4.65) * mm, v(-45.21, 8.57) * mm]});
            skFitSpline(sketch, "E260", {"points": [v(-45.21, 8.57) * mm, v(-45.3, 15.95) * mm, v(-45.4, 23.33) * mm, v(-45.49, 30.71) * mm]});
            skFitSpline(sketch, "E261", {"points": [v(-45.49, 30.71) * mm, v(-45.59, 38.84) * mm, v(-45.69, 46.97) * mm, v(-45.78, 55.1) * mm]});
            skFitSpline(sketch, "E262", {"points": [v(-45.78, 55.1) * mm, v(-45.81, 57.47) * mm, v(-47.14, 75.71) * mm, v(-45.15, 75.91) * mm]});
            skFitSpline(sketch, "E263", {"points": [v(3.23, -103.9) * mm, v(-9.87, -106.42) * mm, v(-24.92, -103.41) * mm, v(-35.45, -95.07) * mm]});
            skFitSpline(sketch, "E264", {"points": [v(-35.45, -95.07) * mm, v(-55.9, -78.88) * mm, v(-56.47, -45.4) * mm, v(-35.9, -29.03) * mm]});
            skFitSpline(sketch, "E265", {"points": [v(-35.9, -29.03) * mm, v(-25.44, -20.7) * mm, v(-10.77, -17.36) * mm, v(2.34, -19.6) * mm]});
            skFitSpline(sketch, "E266", {"points": [v(2.34, -19.6) * mm, v(8.86, -20.7) * mm, v(15.14, -23.18) * mm, v(20.32, -27.33) * mm]});
            skFitSpline(sketch, "E267", {"points": [v(20.32, -27.33) * mm, v(22.73, -29.26) * mm, v(24.89, -31.52) * mm, v(26.75, -33.99) * mm]});
            skFitSpline(sketch, "E268", {"points": [v(26.75, -33.99) * mm, v(28, -35.63) * mm, v(31.49, -39.55) * mm, v(31.37, -41.75) * mm]});
            skFitSpline(sketch, "E269", {"points": [v(31.37, -41.75) * mm, v(31.26, -43.76) * mm, v(27.92, -44.56) * mm, v(26.35, -45.31) * mm]});
            skFitSpline(sketch, "E270", {"points": [v(26.35, -45.31) * mm, v(22.31, -47.25) * mm, v(18.27, -49.17) * mm, v(14.25, -51.13) * mm]});
            skFitSpline(sketch, "E271", {"points": [v(14.25, -51.13) * mm, v(13.37, -51.56) * mm, v(11.55, -53.03) * mm, v(10.57, -52.59) * mm]});
            skFitSpline(sketch, "E272", {"points": [v(10.57, -52.59) * mm, v(10.11, -52.38) * mm, v(9.72, -51.75) * mm, v(9.39, -51.08) * mm]});
            skFitSpline(sketch, "E273", {"points": [v(9.39, -51.08) * mm, v(9.05, -50.4) * mm, v(8.76, -49.67) * mm, v(8.51, -49.28) * mm]});
            skFitSpline(sketch, "E274", {"points": [v(8.51, -49.28) * mm, v(6.78, -46.55) * mm, v(4.3, -44.3) * mm, v(1.4, -42.88) * mm]});
            skFitSpline(sketch, "E275", {"points": [v(1.4, -42.88) * mm, v(-9.61, -37.44) * mm, v(-22.5, -45.3) * mm, v(-25.05, -56.67) * mm]});
            skFitSpline(sketch, "E276", {"points": [v(-25.05, -56.67) * mm, v(-28, -69.83) * mm, v(-18.51, -83.93) * mm, v(-4.16, -82.49) * mm]});
            skFitSpline(sketch, "E277", {"points": [v(-4.16, -82.49) * mm, v(-1.07, -82.18) * mm, v(1.89, -81) * mm, v(4.34, -79.1) * mm]});
            skFitSpline(sketch, "E278", {"points": [v(4.34, -79.1) * mm, v(5.56, -78.15) * mm, v(6.65, -77.04) * mm, v(7.59, -75.82) * mm]});
            skFitSpline(sketch, "E279", {"points": [v(7.59, -75.82) * mm, v(8.53, -74.6) * mm, v(9.08, -72.6) * mm, v(10.1, -71.55) * mm]});
            skFitSpline(sketch, "E280", {"points": [v(10.1, -71.55) * mm, v(12.1, -69.52) * mm, v(18.53, -73.8) * mm, v(20.95, -74.88) * mm]});
            skFitSpline(sketch, "E281", {"points": [v(20.95, -74.88) * mm, v(22.66, -75.64) * mm, v(32.86, -79.02) * mm, v(31.9, -81.07) * mm]});
            skFitSpline(sketch, "E282", {"points": [v(31.9, -81.07) * mm, v(26.3, -92.93) * mm, v(16.23, -101.41) * mm, v(3.23, -103.9) * mm]});
            skFitSpline(sketch, "E283", {"points": [v(39.52, 6.1) * mm, v(39.48, 10.25) * mm, v(39.44, 14.4) * mm, v(39.4, 18.55) * mm]});
            skFitSpline(sketch, "E284", {"points": [v(39.4, 18.55) * mm, v(39.3, 27.21) * mm, v(39.2, 35.87) * mm, v(39.1, 44.53) * mm]});
            skFitSpline(sketch, "E285", {"points": [v(39.1, 44.53) * mm, v(39, 51.96) * mm, v(38.9, 59.4) * mm, v(38.8, 66.84) * mm]});
            skFitSpline(sketch, "E286", {"points": [v(38.8, 66.84) * mm, v(38.77, 68.71) * mm, v(38.74, 70.6) * mm, v(38.72, 72.47) * mm]});
            skFitSpline(sketch, "E287", {"points": [v(38.72, 72.47) * mm, v(38.7, 73.04) * mm, v(38.27, 75.46) * mm, v(38.78, 76.04) * mm]});
            skFitSpline(sketch, "E288", {"points": [v(38.78, 76.04) * mm, v(40.02, 77.46) * mm, v(44.3, 76.65) * mm, v(46.1, 76.67) * mm]});
            skFitSpline(sketch, "E289", {"points": [v(46.1, 76.67) * mm, v(49.7, 76.71) * mm, v(53.3, 76.75) * mm, v(56.9, 76.8) * mm]});
            skFitSpline(sketch, "E290", {"points": [v(56.9, 76.8) * mm, v(58.44, 76.83) * mm, v(60.08, 77.02) * mm, v(61.62, 76.89) * mm]});
            skFitSpline(sketch, "E291", {"points": [v(61.62, 76.89) * mm, v(62.73, 76.8) * mm, v(63.27, 76.63) * mm, v(63.53, 76.21) * mm]});
            skFitSpline(sketch, "E292", {"points": [v(63.53, 76.21) * mm, v(63.8, 75.8) * mm, v(63.8, 75.13) * mm, v(63.84, 74.03) * mm]});
            skFitSpline(sketch, "E293", {"points": [v(63.84, 74.03) * mm, v(64.16, 66.37) * mm, v(64.02, 58.66) * mm, v(64.12, 51) * mm]});
            skFitSpline(sketch, "E294", {"points": [v(64.12, 51) * mm, v(64.3, 35.89) * mm, v(64.47, 20.78) * mm, v(64.68, 5.66) * mm]});
            skFitSpline(sketch, "E295", {"points": [v(64.68, 5.66) * mm, v(64.73, 2.2) * mm, v(64.78, -1.26) * mm, v(64.85, -4.72) * mm]});
            skFitSpline(sketch, "E296", {"points": [v(64.85, -4.72) * mm, v(63.9, -7.05) * mm, v(58.94, -5.96) * mm, v(56.81, -6) * mm]});
            skFitSpline(sketch, "E297", {"points": [v(56.81, -6) * mm, v(53.74, -6.05) * mm, v(50.74, -6.12) * mm, v(47.68, -6.14) * mm]});
            skFitSpline(sketch, "E298", {"points": [v(47.68, -6.14) * mm, v(45.86, -6.15) * mm, v(41.06, -7.07) * mm, v(39.82, -5.54) * mm]});
            skFitSpline(sketch, "E299", {"points": [v(39.82, -5.54) * mm, v(39.05, -4.6) * mm, v(39.6, -1.05) * mm, v(39.58, 0.1) * mm]});
            skFitSpline(sketch, "E300", {"points": [v(39.58, 0.1) * mm, v(39.56, 2.1) * mm, v(39.54, 4.1) * mm, v(39.52, 6.1) * mm]});
            skFitSpline(sketch, "E301", {"points": [v(64.02, -102.17) * mm, v(60.37, -102.2) * mm, v(56.73, -102.22) * mm, v(53.08, -102.27) * mm]});
            skFitSpline(sketch, "E302", {"points": [v(53.08, -102.27) * mm, v(49.24, -102.32) * mm, v(45.4, -102.37) * mm, v(41.56, -102.46) * mm]});
            skFitSpline(sketch, "E303", {"points": [v(41.56, -102.46) * mm, v(39.49, -101.55) * mm, v(40.4, -97.7) * mm, v(40.37, -95.83) * mm]});
            skFitSpline(sketch, "E304", {"points": [v(40.37, -95.83) * mm, v(40.34, -92) * mm, v(40.3, -88.17) * mm, v(40.26, -84.35) * mm]});
            skFitSpline(sketch, "E305", {"points": [v(40.26, -84.35) * mm, v(40.12, -70.45) * mm, v(39.95, -56.56) * mm, v(39.76, -42.67) * mm]});
            skFitSpline(sketch, "E306", {"points": [v(39.76, -42.67) * mm, v(39.67, -35.97) * mm, v(39.49, -29.26) * mm, v(39.46, -22.56) * mm]});
            skFitSpline(sketch, "E307", {"points": [v(39.46, -22.56) * mm, v(39.45, -19.18) * mm, v(40.89, -19.6) * mm, v(43.98, -19.6) * mm]});
            skFitSpline(sketch, "E308", {"points": [v(43.98, -19.6) * mm, v(45.9, -19.58) * mm, v(47.8, -19.56) * mm, v(49.72, -19.54) * mm]});
            skFitSpline(sketch, "E309", {"points": [v(49.72, -19.54) * mm, v(51.63, -19.52) * mm, v(53.54, -19.5) * mm, v(55.45, -19.47) * mm]});
            skFitSpline(sketch, "E310", {"points": [v(55.45, -19.47) * mm, v(57.27, -19.44) * mm, v(62.83, -18.36) * mm, v(64.22, -19.67) * mm]});
            skFitSpline(sketch, "E311", {"points": [v(64.22, -19.67) * mm, v(65.12, -20.51) * mm, v(64.64, -22.78) * mm, v(64.65, -23.87) * mm]});
            skFitSpline(sketch, "E312", {"points": [v(64.65, -23.87) * mm, v(64.68, -26.2) * mm, v(64.7, -28.54) * mm, v(64.73, -30.88) * mm]});
            skFitSpline(sketch, "E313", {"points": [v(64.73, -30.88) * mm, v(64.82, -38.58) * mm, v(64.92, -46.29) * mm, v(65.02, -54) * mm]});
            skFitSpline(sketch, "E314", {"points": [v(65.02, -54) * mm, v(65.12, -62.56) * mm, v(65.23, -71.13) * mm, v(65.33, -79.7) * mm]});
            skFitSpline(sketch, "E315", {"points": [v(65.33, -79.7) * mm, v(65.38, -83.85) * mm, v(65.43, -88) * mm, v(65.5, -92.15) * mm]});
            skFitSpline(sketch, "E316", {"points": [v(65.5, -92.15) * mm, v(65.52, -94.19) * mm, v(66.99, -102.15) * mm, v(64.02, -102.17) * mm]});
            skFitSpline(sketch, "E317", {"points": [v(77.84, 77.33) * mm, v(80.2, 78.28) * mm, v(84.58, 77.51) * mm, v(87.14, 77.54) * mm]});
            skFitSpline(sketch, "E318", {"points": [v(87.14, 77.54) * mm, v(90.46, 77.57) * mm, v(93.77, 77.6) * mm, v(97.09, 77.64) * mm]});
            skFitSpline(sketch, "E319", {"points": [v(97.09, 77.64) * mm, v(103.72, 77.72) * mm, v(110.35, 77.8) * mm, v(116.98, 77.87) * mm]});
            skFitSpline(sketch, "E320", {"points": [v(116.98, 77.87) * mm, v(123.62, 77.95) * mm, v(130.25, 78.1) * mm, v(136.88, 78.13) * mm]});
            skFitSpline(sketch, "E321", {"points": [v(136.88, 78.13) * mm, v(139.84, 78.14) * mm, v(140.1, 77.76) * mm, v(140.14, 74.84) * mm]});
            skFitSpline(sketch, "E322", {"points": [v(140.14, 74.84) * mm, v(140.2, 69.04) * mm, v(140.22, 63.24) * mm, v(140.49, 57.43) * mm]});
            skFitSpline(sketch, "E323", {"points": [v(140.49, 57.43) * mm, v(139.67, 55.2) * mm, v(135.2, 56.21) * mm, v(133.17, 56.2) * mm]});
            skFitSpline(sketch, "E324", {"points": [v(133.17, 56.2) * mm, v(126.68, 56.14) * mm, v(120.2, 56.06) * mm, v(113.72, 55.98) * mm]});
            skFitSpline(sketch, "E325", {"points": [v(113.72, 55.98) * mm, v(110.75, 55.95) * mm, v(107.63, 56.2) * mm, v(104.69, 55.89) * mm]});
            skFitSpline(sketch, "E326", {"points": [v(104.69, 55.89) * mm, v(101.58, 55.56) * mm, v(102.66, 53.26) * mm, v(102.72, 50.57) * mm]});
            skFitSpline(sketch, "E327", {"points": [v(102.72, 50.57) * mm, v(102.78, 47.5) * mm, v(103.53, 47.62) * mm, v(106.48, 47.68) * mm]});
            skFitSpline(sketch, "E328", {"points": [v(106.48, 47.68) * mm, v(110, 47.76) * mm, v(113.53, 47.77) * mm, v(117.06, 47.81) * mm]});
            skFitSpline(sketch, "E329", {"points": [v(117.06, 47.81) * mm, v(123.55, 47.89) * mm, v(130.04, 48.04) * mm, v(136.53, 48.07) * mm]});
            skFitSpline(sketch, "E330", {"points": [v(136.53, 48.07) * mm, v(139.6, 48.08) * mm, v(139.63, 47.38) * mm, v(139.65, 44.45) * mm]});
            skFitSpline(sketch, "E331", {"points": [v(139.65, 44.45) * mm, v(139.66, 41.12) * mm, v(139.7, 37.78) * mm, v(139.73, 34.44) * mm]});
            skFitSpline(sketch, "E332", {"points": [v(139.73, 34.44) * mm, v(139.76, 32.76) * mm, v(140.72, 28.13) * mm, v(139.64, 26.77) * mm]});
            skFitSpline(sketch, "E333", {"points": [v(139.64, 26.77) * mm, v(138.43, 25.27) * mm, v(132.93, 26.14) * mm, v(131.19, 26.12) * mm]});
            skFitSpline(sketch, "E334", {"points": [v(131.19, 26.12) * mm, v(124.6, 26.05) * mm, v(118.02, 25.96) * mm, v(111.44, 25.89) * mm]});
            skFitSpline(sketch, "E335", {"points": [v(111.44, 25.89) * mm, v(109.69, 25.87) * mm, v(104.74, 26.73) * mm, v(103.48, 25.6) * mm]});
            skFitSpline(sketch, "E336", {"points": [v(103.48, 25.6) * mm, v(102.11, 24.38) * mm, v(103.06, 19.1) * mm, v(103.08, 17.43) * mm]});
            skFitSpline(sketch, "E337", {"points": [v(103.08, 17.43) * mm, v(103.16, 10.96) * mm, v(103.28, 4.49) * mm, v(103.33, -1.98) * mm]});
            skFitSpline(sketch, "E338", {"points": [v(103.33, -1.98) * mm, v(103.35, -4.35) * mm, v(103.32, -4.96) * mm, v(100.91, -5.12) * mm]});
            skFitSpline(sketch, "E339", {"points": [v(100.91, -5.12) * mm, v(97.4, -5.34) * mm, v(93.79, -5.18) * mm, v(90.26, -5.22) * mm]});
            skFitSpline(sketch, "E340", {"points": [v(90.26, -5.22) * mm, v(86.24, -5.27) * mm, v(82.22, -5.4) * mm, v(78.2, -5.3) * mm]});
            skFitSpline(sketch, "E341", {"points": [v(78.2, -5.3) * mm, v(77.99, 9.55) * mm, v(77.88, 24.39) * mm, v(77.7, 39.23) * mm]});
            skFitSpline(sketch, "E342", {"points": [v(77.7, 39.23) * mm, v(77.61, 46.16) * mm, v(77.51, 53.08) * mm, v(77.42, 60) * mm]});
            skFitSpline(sketch, "E343", {"points": [v(77.42, 60) * mm, v(77.38, 63.04) * mm, v(77.34, 66.07) * mm, v(77.3, 69.1) * mm]});
            skFitSpline(sketch, "E344", {"points": [v(77.3, 69.1) * mm, v(77.28, 70.4) * mm, v(76.38, 76.74) * mm, v(77.84, 77.33) * mm]});
            skFitSpline(sketch, "E345", {"points": [v(147.2, -100.79) * mm, v(144.66, -100.82) * mm, v(142.12, -100.85) * mm, v(139.59, -100.88) * mm]});
            skFitSpline(sketch, "E346", {"points": [v(139.59, -100.88) * mm, v(138.14, -100.9) * mm, v(135.37, -101.52) * mm, v(134.21, -100.44) * mm]});
            skFitSpline(sketch, "E347", {"points": [v(134.21, -100.44) * mm, v(131.94, -98.31) * mm, v(133.53, -92.44) * mm, v(130.1, -91.39) * mm]});
            skFitSpline(sketch, "E348", {"points": [v(130.1, -91.39) * mm, v(128.32, -90.85) * mm, v(125.21, -91.41) * mm, v(123.36, -91.44) * mm]});
            skFitSpline(sketch, "E349", {"points": [v(123.36, -91.44) * mm, v(120.77, -91.47) * mm, v(118.18, -91.5) * mm, v(115.6, -91.52) * mm]});
            skFitSpline(sketch, "E350", {"points": [v(115.6, -91.52) * mm, v(111.17, -91.57) * mm, v(106.75, -91.6) * mm, v(102.33, -91.63) * mm]});
            skFitSpline(sketch, "E351", {"points": [v(102.33, -91.63) * mm, v(98.81, -93.13) * mm, v(101.24, -100.16) * mm, v(97.72, -101.47) * mm]});
            skFitSpline(sketch, "E352", {"points": [v(97.72, -101.47) * mm, v(93.34, -101.5) * mm, v(88.95, -101.54) * mm, v(84.56, -101.58) * mm]});
            skFitSpline(sketch, "E353", {"points": [v(84.56, -101.58) * mm, v(79.77, -101.63) * mm, v(74.94, -101.85) * mm, v(70.15, -101.64) * mm]});
            skFitSpline(sketch, "E354", {"points": [v(70.15, -101.64) * mm, v(77.87, -79.22) * mm, v(86, -56.94) * mm, v(93.95, -34.6) * mm]});
            skFitSpline(sketch, "E355", {"points": [v(93.95, -34.6) * mm, v(95.73, -29.59) * mm, v(97.5, -24.58) * mm, v(99.25, -19.55) * mm]});
            skFitSpline(sketch, "E356", {"points": [v(99.25, -19.55) * mm, v(100.54, -17.87) * mm, v(103.33, -18.51) * mm, v(105.22, -18.5) * mm]});
            skFitSpline(sketch, "E357", {"points": [v(105.22, -18.5) * mm, v(108.4, -18.47) * mm, v(111.58, -18.44) * mm, v(114.76, -18.41) * mm]});
            skFitSpline(sketch, "E358", {"points": [v(114.76, -18.41) * mm, v(117.48, -18.39) * mm, v(120.2, -18.36) * mm, v(122.93, -18.32) * mm]});
            skFitSpline(sketch, "E359", {"points": [v(122.93, -18.32) * mm, v(124.96, -18.3) * mm, v(128.94, -17.46) * mm, v(130.75, -18.43) * mm]});
            skFitSpline(sketch, "E360", {"points": [v(130.75, -18.43) * mm, v(131.64, -18.9) * mm, v(131.73, -19.68) * mm, v(132.1, -20.5) * mm]});
            skFitSpline(sketch, "E361", {"points": [v(132.1, -20.5) * mm, v(135.4, -27.7) * mm, v(137.83, -35.45) * mm, v(140.66, -42.85) * mm]});
            skFitSpline(sketch, "E362", {"points": [v(140.66, -42.85) * mm, v(144.8, -53.7) * mm, v(148.96, -64.53) * mm, v(153.1, -75.38) * mm]});
            skFitSpline(sketch, "E363", {"points": [v(153.1, -75.38) * mm, v(156.32, -83.78) * mm, v(159.54, -92.2) * mm, v(162.77, -100.6) * mm]});
            skFitSpline(sketch, "E364", {"points": [v(162.77, -100.6) * mm, v(157.58, -100.66) * mm, v(152.38, -100.72) * mm, v(147.2, -100.79) * mm]});
            skFitSpline(sketch, "E365", {"points": [v(157.29, 56.12) * mm, v(154.13, 56.08) * mm, v(150.96, 56.03) * mm, v(147.8, 55.95) * mm]});
            skFitSpline(sketch, "E366", {"points": [v(147.8, 55.95) * mm, v(144.74, 55.88) * mm, v(146.06, 65.9) * mm, v(146.03, 68.17) * mm]});
            skFitSpline(sketch, "E367", {"points": [v(146.03, 68.17) * mm, v(145.97, 71.39) * mm, v(145.84, 74.6) * mm, v(145.88, 77.82) * mm]});
            skFitSpline(sketch, "E368", {"points": [v(145.88, 77.82) * mm, v(157.06, 78.15) * mm, v(168.26, 78.16) * mm, v(179.45, 78.3) * mm]});
            skFitSpline(sketch, "E369", {"points": [v(179.45, 78.3) * mm, v(189.32, 78.42) * mm, v(199.2, 78.52) * mm, v(209.06, 78.65) * mm]});
            skFitSpline(sketch, "E370", {"points": [v(209.06, 78.65) * mm, v(210.4, 78.67) * mm, v(213.93, 79.39) * mm, v(214.99, 78.42) * mm]});
            skFitSpline(sketch, "E371", {"points": [v(214.99, 78.42) * mm, v(215.92, 77.56) * mm, v(215.39, 74.38) * mm, v(215.4, 73.18) * mm]});
            skFitSpline(sketch, "E372", {"points": [v(215.4, 73.18) * mm, v(215.43, 70.47) * mm, v(215.46, 67.76) * mm, v(215.5, 65.05) * mm]});
            skFitSpline(sketch, "E373", {"points": [v(215.5, 65.05) * mm, v(215.52, 63.38) * mm, v(216.5, 58.34) * mm, v(215.25, 57.1) * mm]});
            skFitSpline(sketch, "E374", {"points": [v(215.25, 57.1) * mm, v(214.26, 56.1) * mm, v(211.01, 56.77) * mm, v(209.8, 56.76) * mm]});
            skFitSpline(sketch, "E375", {"points": [v(209.8, 56.76) * mm, v(206.98, 56.75) * mm, v(204.15, 56.72) * mm, v(201.32, 56.68) * mm]});
            skFitSpline(sketch, "E376", {"points": [v(201.32, 56.68) * mm, v(199.84, 56.66) * mm, v(195.52, 57.4) * mm, v(194.32, 56.53) * mm]});
            skFitSpline(sketch, "E377", {"points": [v(194.32, 56.53) * mm, v(193.2, 55.72) * mm, v(193.55, 54.54) * mm, v(193.57, 53.11) * mm]});
            skFitSpline(sketch, "E378", {"points": [v(193.57, 53.11) * mm, v(193.68, 41.92) * mm, v(193.85, 30.73) * mm, v(193.99, 19.54) * mm]});
            skFitSpline(sketch, "E379", {"points": [v(193.99, 19.54) * mm, v(194.05, 14.47) * mm, v(194.1, 9.4) * mm, v(194.15, 4.33) * mm]});
            skFitSpline(sketch, "E380", {"points": [v(194.15, 4.33) * mm, v(194.17, 2.4) * mm, v(195, -1.52) * mm, v(194.2, -3.25) * mm]});
            skFitSpline(sketch, "E381", {"points": [v(194.2, -3.25) * mm, v(193.41, -4.99) * mm, v(191.47, -4.43) * mm, v(189.74, -4.44) * mm]});
            skFitSpline(sketch, "E382", {"points": [v(189.74, -4.44) * mm, v(184.53, -4.46) * mm, v(179.32, -4.53) * mm, v(174.11, -4.62) * mm]});
            skFitSpline(sketch, "E383", {"points": [v(174.11, -4.62) * mm, v(172.6, -4.64) * mm, v(170.14, -5.3) * mm, v(169.2, -3.92) * mm]});
            skFitSpline(sketch, "E384", {"points": [v(169.2, -3.92) * mm, v(168.72, -3.22) * mm, v(169.08, -1.12) * mm, v(169.07, -0.33) * mm]});
            skFitSpline(sketch, "E385", {"points": [v(169.07, -0.33) * mm, v(169.05, 1.55) * mm, v(169.03, 3.43) * mm, v(169.01, 5.3) * mm]});
            skFitSpline(sketch, "E386", {"points": [v(169.01, 5.3) * mm, v(168.88, 17.52) * mm, v(168.73, 29.73) * mm, v(168.6, 41.95) * mm]});
            skFitSpline(sketch, "E387", {"points": [v(168.6, 41.95) * mm, v(168.55, 46.43) * mm, v(168.5, 50.9) * mm, v(168.46, 55.38) * mm]});
            skFitSpline(sketch, "E388", {"points": [v(168.46, 55.38) * mm, v(166.28, 57.5) * mm, v(160.75, 56.18) * mm, v(157.29, 56.12) * mm]});
            skFitSpline(sketch, "E389", {"points": [v(221.9, -100.44) * mm, v(211.95, -100.58) * mm, v(202, -100.71) * mm, v(192.03, -100.81) * mm]});
            skFitSpline(sketch, "E390", {"points": [v(192.03, -100.81) * mm, v(187.48, -100.86) * mm, v(182.92, -100.9) * mm, v(178.36, -100.96) * mm]});
            skFitSpline(sketch, "E391", {"points": [v(178.36, -100.96) * mm, v(175.84, -100.99) * mm, v(168.18, -102.43) * mm, v(166.9, -100) * mm]});
            skFitSpline(sketch, "E392", {"points": [v(166.9, -100) * mm, v(166.14, -98.54) * mm, v(166.8, -95.32) * mm, v(166.78, -93.63) * mm]});
            skFitSpline(sketch, "E393", {"points": [v(166.78, -93.63) * mm, v(166.76, -91.06) * mm, v(166.74, -88.49) * mm, v(166.71, -85.92) * mm]});
            skFitSpline(sketch, "E394", {"points": [v(166.71, -85.92) * mm, v(166.66, -80.79) * mm, v(166.6, -75.65) * mm, v(166.55, -70.51) * mm]});
            skFitSpline(sketch, "E395", {"points": [v(166.55, -70.51) * mm, v(166.44, -60.57) * mm, v(166.33, -50.63) * mm, v(166.19, -40.69) * mm]});
            skFitSpline(sketch, "E396", {"points": [v(166.19, -40.69) * mm, v(166.12, -36.15) * mm, v(166.06, -31.62) * mm, v(166, -27.1) * mm]});
            skFitSpline(sketch, "E397", {"points": [v(166, -27.1) * mm, v(165.96, -24.7) * mm, v(164.67, -19.25) * mm, v(167.17, -18.3) * mm]});
            skFitSpline(sketch, "E398", {"points": [v(167.17, -18.3) * mm, v(172.16, -18.23) * mm, v(177.14, -18.2) * mm, v(182.13, -18.12) * mm]});
            skFitSpline(sketch, "E399", {"points": [v(182.13, -18.12) * mm, v(183.23, -18.1) * mm, v(184.47, -17.96) * mm, v(185.7, -17.87) * mm]});
            skFitSpline(sketch, "E400", {"points": [v(185.7, -17.87) * mm, v(186.93, -17.79) * mm, v(188.15, -17.76) * mm, v(189.23, -17.98) * mm]});
            skFitSpline(sketch, "E401", {"points": [v(189.23, -17.98) * mm, v(191.21, -18.39) * mm, v(191.02, -19.05) * mm, v(191.06, -21.18) * mm]});
            skFitSpline(sketch, "E402", {"points": [v(191.06, -21.18) * mm, v(191.28, -31.06) * mm, v(191.28, -40.95) * mm, v(191.4, -50.83) * mm]});
            skFitSpline(sketch, "E403", {"points": [v(191.4, -50.83) * mm, v(191.47, -55.77) * mm, v(191.53, -60.7) * mm, v(191.6, -65.65) * mm]});
            skFitSpline(sketch, "E404", {"points": [v(191.6, -65.65) * mm, v(191.62, -68) * mm, v(191.65, -70.35) * mm, v(191.68, -72.7) * mm]});
            skFitSpline(sketch, "E405", {"points": [v(191.68, -72.7) * mm, v(191.7, -73.85) * mm, v(191.07, -77.43) * mm, v(191.84, -78.4) * mm]});
            skFitSpline(sketch, "E406", {"points": [v(191.84, -78.4) * mm, v(192.54, -79.3) * mm, v(194.04, -78.93) * mm, v(195.11, -78.91) * mm]});
            skFitSpline(sketch, "E407", {"points": [v(195.11, -78.91) * mm, v(197.94, -78.89) * mm, v(200.77, -78.84) * mm, v(203.6, -78.8) * mm]});
            skFitSpline(sketch, "E408", {"points": [v(203.6, -78.8) * mm, v(209.98, -78.72) * mm, v(216.38, -78.47) * mm, v(222.76, -78.59) * mm]});
            skFitSpline(sketch, "E409", {"points": [v(222.76, -78.59) * mm, v(223.96, -81.1) * mm, v(223.32, -84.84) * mm, v(223.36, -87.8) * mm]});
            skFitSpline(sketch, "E410", {"points": [v(223.36, -87.8) * mm, v(223.38, -90.03) * mm, v(224.87, -100.4) * mm, v(221.9, -100.44) * mm]});
            skSolve(sketch);
        }
        {
            var Q0;
            Q0 = qSketchRegion(id + "F0", true);
            extrude(context, id + "F1", {"entities" : qUnion([Q0]), "depth" : 12 * mm, "offsetDistance" : 25 * mm});
        }
    });
